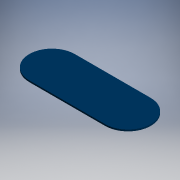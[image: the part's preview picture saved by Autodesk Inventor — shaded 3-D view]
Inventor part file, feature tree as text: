
AUTODESK INVENTOR PART (.ipt)
format: ipt  version: 2017.3 (Build 213256000, 256)  size: 231,936 bytes
history: native  units: mm (DEFAULTED — no unit token found)
features: sketch x10, extrude x9, other x7, hole x1
ambient origin geometry x8: Origin, YZ Plane, XZ Plane, XY Plane, X Axis, Y Axis, Z Axis, Center Point
bodies: Solid1 (feature_tree)
feature tree (27):
  extrude  "Extrusion1"  Depth=0.05mm TaperAngle=0.0deg
  extrude  "Extrusion2"  Depth=0.05mm TaperAngle=0.0deg
  extrude  "Extrusion3"  Depth=0.05mm TaperAngle=0.0deg
  extrude  "Extrusion4"  Depth=0.05mm TaperAngle=0.0deg
  extrude  "Extrusion5"  TaperAngle=0.0deg  [1 undecoded]
  extrude  "Extrusion6"  [1 undecoded]
  extrude  "Extrusion7"  [1 undecoded]
  hole  "Hole1"  [1 undecoded]
  extrude  "Extrusion8"  [1 undecoded]
  extrude  "Extrusion9"  [1 undecoded]
  other  "aluschild_XY"
  other  "aluschild_YZ"
  other  "aluschild_ZX"
  other  "aluschild_X"
  other  "aluschild_Y"
  other  "aluschild_Z"
  other  "aluschild_Center"
  sketch  "Sketch_1"  dims[d0=0.3mm d1=0.0mm d2=0.05mm d3=0.0mm]
  sketch  "Sketch_13"
  sketch  "Sketch_15"
  sketch  "Sketch_16"
  sketch  "Sketch_5"  dims[d12=0.05mm d13=0.0mm]
  sketch  "Sketch_6"  dims[d14=1.344mm d15=6.0mm d16=4.0mm d17=2.0mm d18=90.0deg d19=0.05mm d20=0.0mm d21=0.05mm d22=0.0mm]
  sketch  "Sketch_7"  dims[d23=0.05mm d24=0.0mm d25=0.0mm]
  sketch  "Sketch8"
  sketch  "Sketch_3"  dims[d4=0.05mm d5=0.0mm d6=0.05mm d7=0.0mm]
  sketch  "Sketch_4"  dims[d8=0.05mm d9=0.0mm d10=0.05mm d11=0.0mm]
note: 6 required parameter values undecoded (feature->parameter linkage not recoverable at this tier; creation-order binding heuristic only, values carry confidence <= 0.55)
